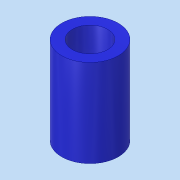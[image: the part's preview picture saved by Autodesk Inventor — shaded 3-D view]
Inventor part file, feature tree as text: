
AUTODESK INVENTOR PART (.ipt)
format: ipt  version: 2018 (Build 220112000, 112)  size: 83,456 bytes
history: native  units: mm
features: extrude x1, sketch x1
ambient origin geometry x8: Origin, YZ Plane, XZ Plane, XY Plane, X Axis, Y Axis, Z Axis, Center Point
bodies: Volumenkörper1 (feature_tree)
feature tree (2):
  extrude  "Extrusion1"  Depth=6.2mm
  sketch  "Skizze1"  dims[d0=2.5mm d1=4.0mm d2=6.2mm d3=0.0mm]
